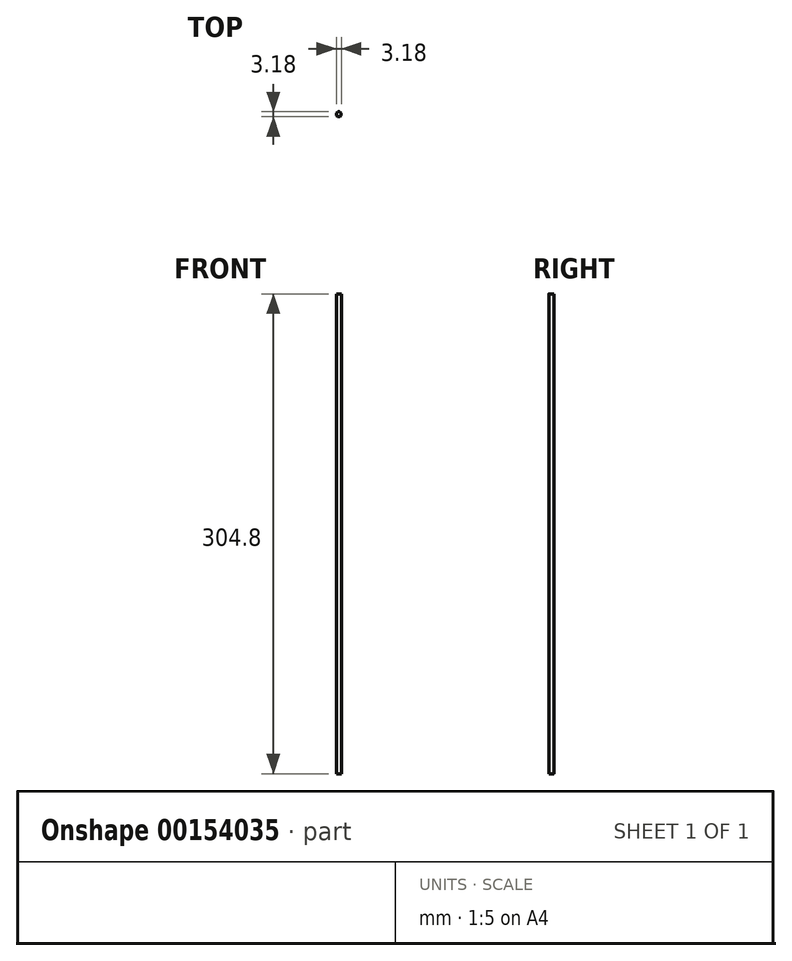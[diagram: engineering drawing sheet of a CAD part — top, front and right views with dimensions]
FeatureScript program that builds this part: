
annotation { "Feature Type Name" : "Feature", "Feature Type Description" : "" }
export const myFeature = defineFeature(function(context is Context, id is Id, definition is map)
    precondition{}
    {
        {
            var Q0;
            Q0=qCreatedBy(makeId("Top.planeOp"),FACE);
            var sketch = newSketch(context, id + "F0", { "sketchPlane" : qUnion([Q0])});
            skCircle(sketch, "E0", {"center": v(0, 0) * mm, "radius": 1.59 * mm});
            skSolve(sketch);
        }
        {
            var Q0;
            Q0=makeQuery(id+"F0.imprint","IMPRINT",FACE,{"disambiguationData":[TD([[makeQuery(id+"F0.imprint","IMPRINT",EDGE,{"derivedFrom":sQuery(id+"F0.wireOp",EDGE,"E0")}),1.0]])]});
            extrude(context, id + "F1", {"entities" : qUnion([Q0]), "depth" : 304.8 * mm});
        }
    });
